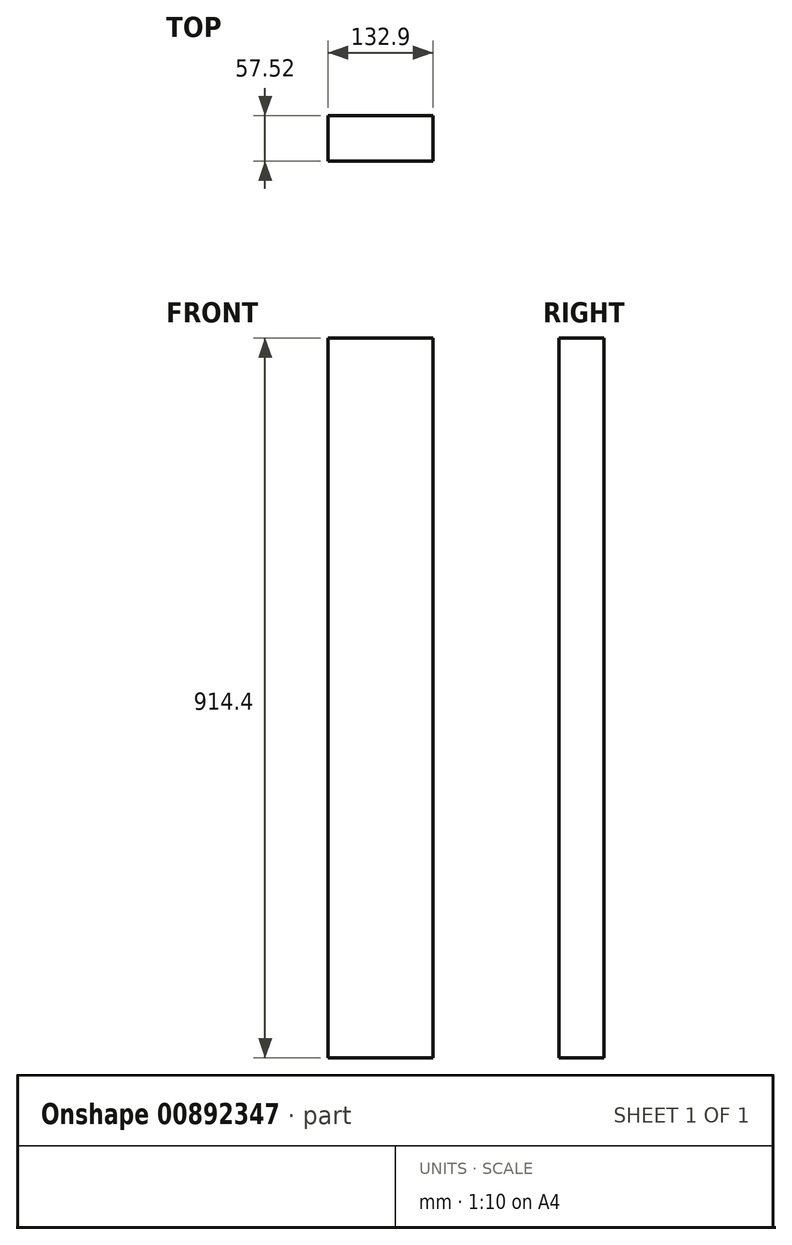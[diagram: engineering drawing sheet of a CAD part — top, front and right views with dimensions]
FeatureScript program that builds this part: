
annotation { "Feature Type Name" : "Feature", "Feature Type Description" : "" }
export const myFeature = defineFeature(function(context is Context, id is Id, definition is map)
    precondition{}
    {
        {
            var Q0;
            Q0=qCreatedBy(makeId("Top.planeOp"),FACE);
            var sketch = newSketch(context, id + "F0", { "sketchPlane" : qUnion([Q0])});
            skLineSegment(sketch, "E0.bottom", {"start": v(-66.45, 28.76) * mm, "end": v(66.45, 28.76) * mm});
            skLineSegment(sketch, "E0.top", {"start": v(-66.45, -28.76) * mm, "end": v(66.45, -28.76) * mm});
            skLineSegment(sketch, "E0.left", {"start": v(-66.45, 28.76) * mm, "end": v(-66.45, -28.76) * mm});
            skLineSegment(sketch, "E0.right", {"start": v(66.45, 28.76) * mm, "end": v(66.45, -28.76) * mm});
            skPoint(sketch, "E0.middle", {"position": v(0, 0) * mm});
            skSolve(sketch);
        }
        {
            var Q0;
            Q0=makeQuery(id+"F0.imprint","IMPRINT",FACE,{"disambiguationData":[TD([[makeQuery(id+"F0.imprint","IMPRINT",EDGE,{"derivedFrom":sQuery(id+"F0.wireOp",EDGE,"E0.bottom")}),-1.0]])]});
            extrude(context, id + "F1", {"entities" : qUnion([Q0]), "depth" : 914.4 * mm, "offsetDistance" : 25.4 * mm});
        }
    });
